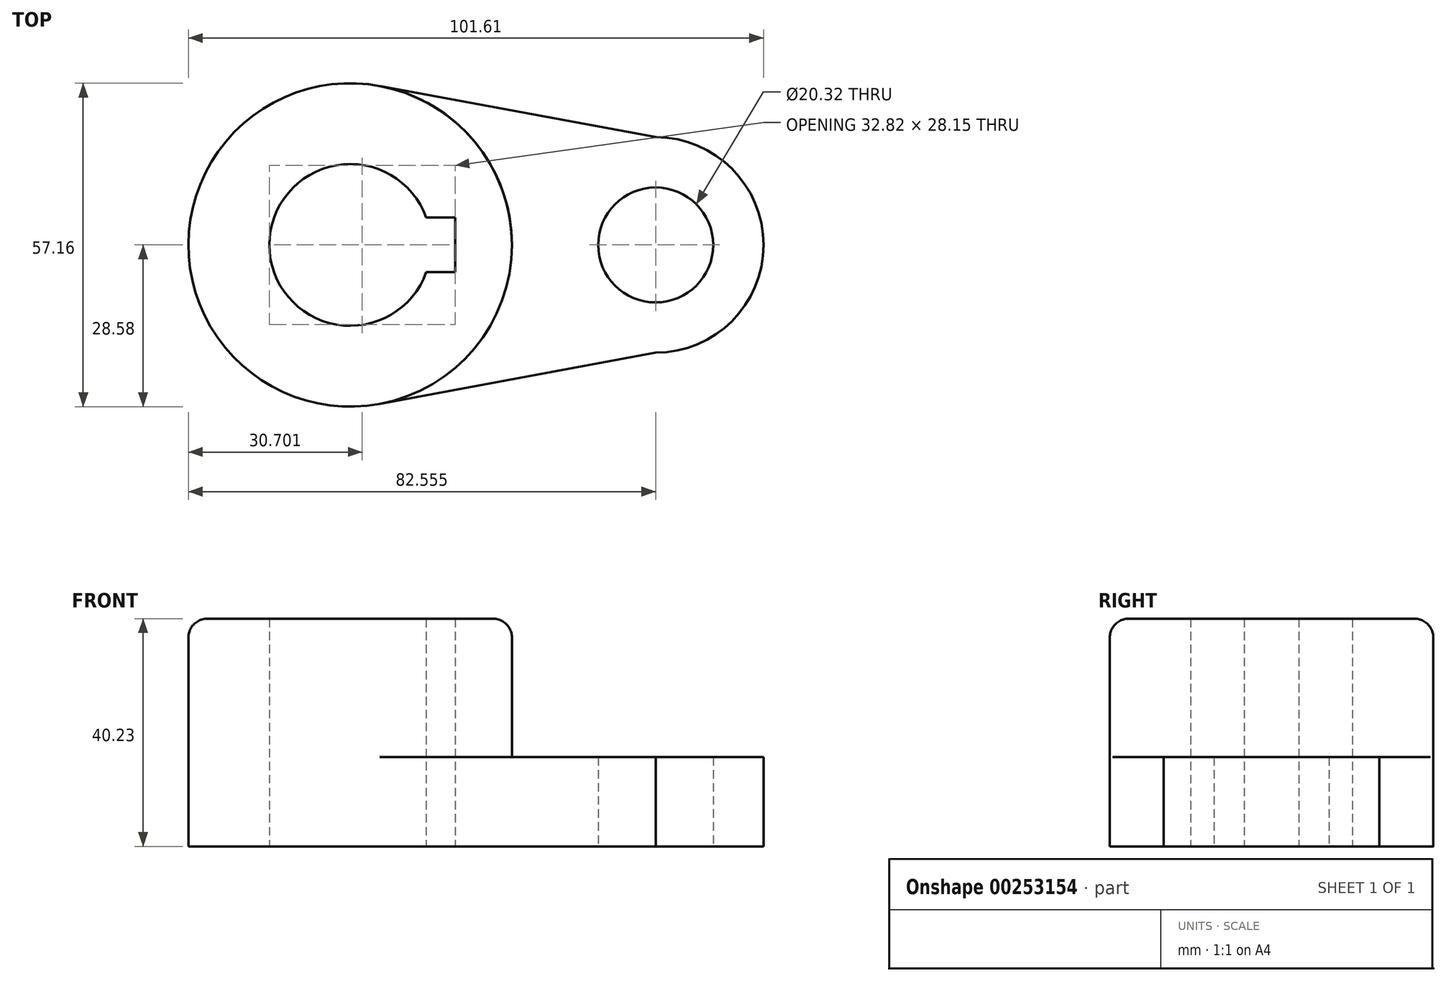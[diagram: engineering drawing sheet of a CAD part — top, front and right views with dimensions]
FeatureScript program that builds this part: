
annotation { "Feature Type Name" : "Feature", "Feature Type Description" : "" }
export const myFeature = defineFeature(function(context is Context, id is Id, definition is map)
    precondition{}
    {
        {
            var Q0;
            Q0=qCreatedBy(makeId("Top.planeOp"),FACE);
            var sketch = newSketch(context, id + "F0", { "sketchPlane" : qUnion([Q0])});
            skCircle(sketch, "E0", {"center": v(0, 0) * mm, "radius": 28.58 * mm});
            skCircle(sketch, "E1", {"center": v(0, 0) * mm, "radius": 14.29 * mm});
            skCircle(sketch, "E2", {"center": v(53.98, 0) * mm, "radius": 10.16 * mm});
            skLineSegment(sketch, "E3.bottom", {"start": v(18.53, -4.83) * mm, "end": v(-18.53, -4.83) * mm});
            skLineSegment(sketch, "E3.top", {"start": v(18.53, 4.83) * mm, "end": v(-18.53, 4.83) * mm});
            skLineSegment(sketch, "E3.left", {"start": v(18.53, -4.83) * mm, "end": v(18.53, 4.83) * mm});
            skLineSegment(sketch, "E3.right", {"start": v(-18.53, -4.83) * mm, "end": v(-18.53, 4.83) * mm});
            skLineSegment(sketch, "E4", {"start": v(53.98, 19.05) * mm, "end": v(0, 29.06) * mm});
            skLineSegment(sketch, "E5", {"start": v(53.98, -19.05) * mm, "end": v(0, -29.06) * mm});
            skArc(sketch, "E6", {"start": v(53.98, 19.05) * mm, "mid": v(67.45, 13.47) * mm, "end": v(73.03, 0) * mm});
            skArc(sketch, "E7", {"start": v(73.03, 0) * mm, "mid": v(67.45, -13.47) * mm, "end": v(53.98, -19.05) * mm});
            skSolve(sketch);
        }
        {
            var Q0;
            {var subQ5=sQuery(id+"F0.wireOp",EDGE,"E3.right");Q0=makeQuery(id+"F0.imprint","IMPRINT",FACE,{"disambiguationData":[TD([[makeQuery(id+"F0.imprint","IMPRINT",EDGE,{"derivedFrom":subQ5}),-1.0]])]});}
            var Q1;
            {var subQ11=sQuery(id+"F0.wireOp",EDGE,"E3.left");Q1=makeQuery(id+"F0.imprint","IMPRINT",FACE,{"disambiguationData":[TD([[makeQuery(id+"F0.imprint","IMPRINT",EDGE,{"derivedFrom":subQ11}),-1.0]])]});}
            extrude(context, id + "F1", {"entities" : qUnion([Q0, Q1]), "depth" : 40.23 * mm});
        }
        {
            var Q0;
            Q0=makeQuery(id+"F0.imprint","IMPRINT",FACE,{"disambiguationData":[TD([[makeQuery(id+"F0.imprint","IMPRINT",EDGE,{"derivedFrom":sQuery(id+"F0.wireOp",EDGE,"E2")}),-1.0]])]});
            extrude(context, id + "F2", {"entities" : qUnion([Q0]), "operationType" : NewBodyOperationType.ADD, "depth" : 15.77 * mm});
        }
        {
            var Q0;
            Q0=makeQuery(id+"F1.opExtrude","CAP_EDGE",EDGE,{"disambiguationData":[OSD([sQuery(id+"F0.wireOp",EDGE,"E0")])],"isStart":false});
            fillet(context, id + "F3", {"entities" : qUnion([Q0]), "radius" : 3.3 * mm, "tangentPropagation" : true, "allowEdgeOverflow" : false});
        }
    });
